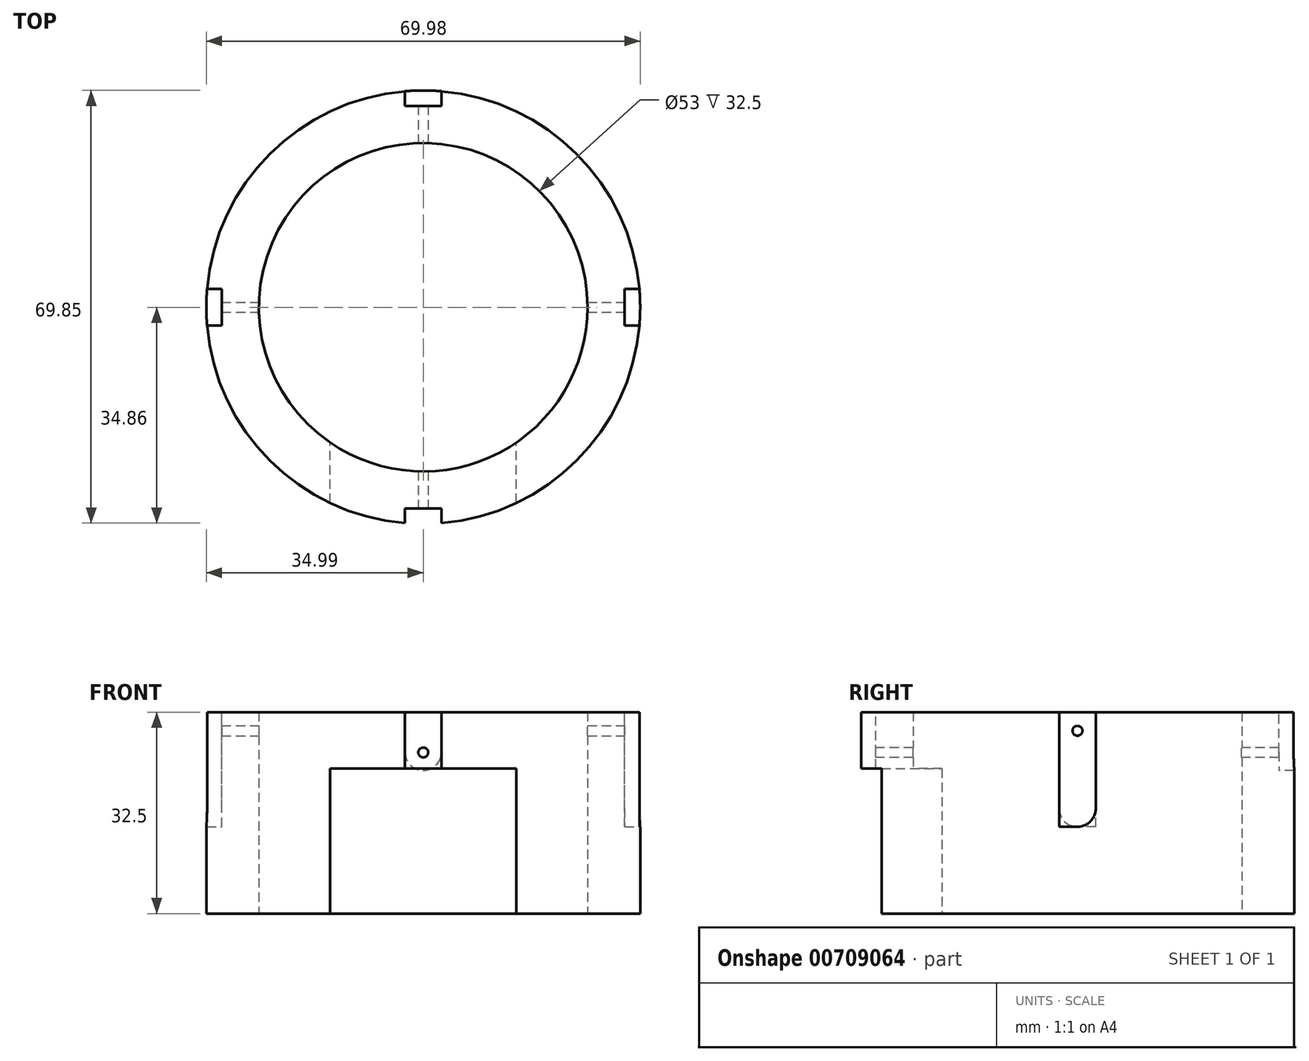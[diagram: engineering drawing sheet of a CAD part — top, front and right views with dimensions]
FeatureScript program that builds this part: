
annotation { "Feature Type Name" : "Feature", "Feature Type Description" : "" }
export const myFeature = defineFeature(function(context is Context, id is Id, definition is map)
    precondition{}
    {
        {
            var Q0;
            Q0=qCreatedBy(makeId("Top.planeOp"),FACE);
            var sketch = newSketch(context, id + "F0", { "sketchPlane" : qUnion([Q0])});
            skCircle(sketch, "E0", {"center": v(0, 0) * mm, "radius": 34.98 * mm});
            skCircle(sketch, "E1", {"center": v(0, 0) * mm, "radius": 26.5 * mm});
            skSolve(sketch);
        }
        {
            var Q0;
            Q0=makeQuery(id+"F0.imprint","IMPRINT",FACE,{"disambiguationData":[TD([[makeQuery(id+"F0.imprint","IMPRINT",EDGE,{"derivedFrom":sQuery(id+"F0.wireOp",EDGE,"E0")}),1.0]])]});
            extrude(context, id + "F1", {"entities" : qUnion([Q0]), "depth" : 32.5 * mm, "offsetDistance" : 25 * mm});
        }
        {
            var Q0;
            Q0=makeQuery(id+"F1.opExtrude","CAP_FACE",FACE,{"disambiguationData":[OSD([sQuery(id+"F0.wireOp",EDGE,"E0"),sQuery(id+"F0.wireOp",EDGE,"E1")])],"isStart":true});
            var sketch = newSketch(context, id + "F2", { "sketchPlane" : qUnion([Q0])});
            skLineSegment(sketch, "E2.bottom", {"start": v(-15.03, 49.64) * mm, "end": v(15.02, 49.64) * mm});
            skLineSegment(sketch, "E2.top", {"start": v(-15.03, 4.75) * mm, "end": v(15.03, 4.75) * mm});
            skLineSegment(sketch, "E2.left", {"start": v(-15.03, 49.64) * mm, "end": v(-15.03, 4.75) * mm});
            skLineSegment(sketch, "E2.right", {"start": v(15.02, 49.64) * mm, "end": v(15.03, 4.75) * mm});
            skSolve(sketch);
        }
        {
            var Q0;
            {var subQ0=sQuery(id+"F2.wireOp",EDGE,"E2.left");var subQ1=makeQuery(id+"F1.opExtrude","CAP_EDGE",EDGE,{"disambiguationData":[OSD([sQuery(id+"F0.wireOp",EDGE,"E0")])],"isStart":true});var subQ2=makeQuery(id+"F2.imprint","INTERSECT",VERTEX,{"derivedFrom":[subQ1,subQ0]});Q0=makeQuery(id+"F2.imprint","IMPRINT",FACE,{"disambiguationData":[TD([[makeQuery(id+"F2.imprint","IMPRINT",EDGE,{"disambiguationData":[TD([[subQ2,-1.0]])],"derivedFrom":subQ0}),1.0]])]});}
            extrude(context, id + "F3", {"entities" : qUnion([Q0]), "operationType" : NewBodyOperationType.REMOVE, "oppositeDirection" : true, "depth" : 23.4 * mm, "offsetDistance" : 25 * mm});
        }
        {
            var Q0;
            Q0=makeQuery(id+"F1.opExtrude","CAP_FACE",FACE,{"disambiguationData":[OSD([sQuery(id+"F0.wireOp",EDGE,"E0"),sQuery(id+"F0.wireOp",EDGE,"E1")])],"isStart":false});
            var sketch = newSketch(context, id + "F4", { "sketchPlane" : qUnion([Q0])});
            skLineSegment(sketch, "E3.bottom", {"start": v(-41.98, 2.95) * mm, "end": v(-32.5, 2.95) * mm});
            skLineSegment(sketch, "E3.top", {"start": v(-41.98, -2.95) * mm, "end": v(-32.5, -2.95) * mm});
            skLineSegment(sketch, "E3.left", {"start": v(-41.98, 2.95) * mm, "end": v(-41.98, -2.95) * mm});
            skLineSegment(sketch, "E3.right", {"start": v(-32.5, 2.95) * mm, "end": v(-32.5, -2.95) * mm});
            skLineSegment(sketch, "E4.bottom", {"start": v(32.5, 2.95) * mm, "end": v(40.96, 2.95) * mm});
            skLineSegment(sketch, "E4.top", {"start": v(32.5, -2.95) * mm, "end": v(40.96, -2.95) * mm});
            skLineSegment(sketch, "E4.left", {"start": v(32.5, 2.95) * mm, "end": v(32.5, -2.95) * mm});
            skLineSegment(sketch, "E4.right", {"start": v(40.96, 2.95) * mm, "end": v(40.96, -2.95) * mm});
            skSolve(sketch);
        }
        {
            var Q0;
            {var subQ0=sQuery(id+"F4.wireOp",EDGE,"E4.left");Q0=makeQuery(id+"F4.imprint","IMPRINT",FACE,{"disambiguationData":[TD([[makeQuery(id+"F4.imprint","IMPRINT",EDGE,{"derivedFrom":subQ0}),1.0]])]});}
            var Q1;
            {var subQ0=sQuery(id+"F4.wireOp",EDGE,"E3.right");Q1=makeQuery(id+"F4.imprint","IMPRINT",FACE,{"disambiguationData":[TD([[makeQuery(id+"F4.imprint","IMPRINT",EDGE,{"derivedFrom":subQ0}),-1.0]])]});}
            extrude(context, id + "F5", {"entities" : qUnion([Q0, Q1]), "operationType" : NewBodyOperationType.REMOVE, "oppositeDirection" : true, "depth" : 18.5 * mm, "offsetDistance" : 25 * mm});
        }
        {
            var Q0;
            Q0=makeQuery(id+"F5.boolean.opBoolean","COPY",EDGE,{"derivedFrom":makeQuery(id+"F5.opExtrude","CAP_EDGE",EDGE,{"disambiguationData":[OSD([sQuery(id+"F4.wireOp",EDGE,"E3.top")])],"isStart":false})});
            var Q1;
            Q1=makeQuery(id+"F5.boolean.opBoolean","COPY",EDGE,{"derivedFrom":makeQuery(id+"F5.opExtrude","CAP_EDGE",EDGE,{"disambiguationData":[OSD([sQuery(id+"F4.wireOp",EDGE,"E4.bottom")])],"isStart":false})});
            fillet(context, id + "F6", {"entities" : qUnion([Q0, Q1]), "radius" : 2.95 * mm, "tangentPropagation" : true, "allowEdgeOverflow" : false});
        }
        {
            var Q0;
            Q0=qCreatedBy(makeId("Right.planeOp"),FACE);
            var sketch = newSketch(context, id + "F7", { "sketchPlane" : qUnion([Q0])});
            skCircle(sketch, "E5", {"center": v(0, 29.5) * mm, "radius": 0.8 * mm});
            skSolve(sketch);
        }
        {
            var Q0;
            Q0 = qSketchRegion(id + "F7", true);
            extrude(context, id + "F8", {"entities" : qUnion([Q0]), "operationType" : NewBodyOperationType.REMOVE, "endBound" : BoundingType.THROUGH_ALL, "oppositeDirection" : true, "depth" : 25 * mm, "offsetDistance" : 25 * mm, "hasSecondDirection" : true, "secondDirectionBound" : SecondDirectionBoundingType.THROUGH_ALL, "secondDirectionOppositeDirection" : false, "secondDirectionDepth" : 25 * mm});
        }
        {
            var Q0;
            Q0=makeQuery(id+"F1.opExtrude","CAP_FACE",FACE,{"disambiguationData":[OSD([sQuery(id+"F0.wireOp",EDGE,"E0"),sQuery(id+"F0.wireOp",EDGE,"E1")])],"isStart":false});
            var sketch = newSketch(context, id + "F9", { "sketchPlane" : qUnion([Q0])});
            skLineSegment(sketch, "E6.bottom", {"start": v(-2.95, 38.61) * mm, "end": v(2.95, 38.61) * mm});
            skLineSegment(sketch, "E6.top", {"start": v(-2.95, 32.5) * mm, "end": v(2.95, 32.5) * mm});
            skLineSegment(sketch, "E6.left", {"start": v(-2.95, 38.61) * mm, "end": v(-2.95, 32.5) * mm});
            skLineSegment(sketch, "E6.right", {"start": v(2.95, 38.61) * mm, "end": v(2.95, 32.5) * mm});
            skLineSegment(sketch, "E7.bottom", {"start": v(-2.95, -39.44) * mm, "end": v(2.95, -39.44) * mm});
            skLineSegment(sketch, "E7.top", {"start": v(-2.95, -32.5) * mm, "end": v(2.95, -32.5) * mm});
            skLineSegment(sketch, "E7.left", {"start": v(-2.95, -39.44) * mm, "end": v(-2.95, -32.5) * mm});
            skLineSegment(sketch, "E7.right", {"start": v(2.95, -39.44) * mm, "end": v(2.95, -32.5) * mm});
            skSolve(sketch);
        }
        {
            var Q0;
            {var subQ0=sQuery(id+"F9.wireOp",EDGE,"E6.top");Q0=makeQuery(id+"F9.imprint","IMPRINT",FACE,{"disambiguationData":[TD([[makeQuery(id+"F9.imprint","IMPRINT",EDGE,{"derivedFrom":subQ0}),1.0]])]});}
            var Q1;
            {var subQ0=sQuery(id+"F9.wireOp",EDGE,"E7.top");Q1=makeQuery(id+"F9.imprint","IMPRINT",FACE,{"disambiguationData":[TD([[makeQuery(id+"F9.imprint","IMPRINT",EDGE,{"derivedFrom":subQ0}),-1.0]])]});}
            extrude(context, id + "F10", {"entities" : qUnion([Q0, Q1]), "operationType" : NewBodyOperationType.REMOVE, "oppositeDirection" : true, "depth" : 9.4 * mm, "offsetDistance" : 25 * mm});
        }
        {
            var Q0;
            Q0=makeQuery(id+"F10.boolean.opBoolean","COPY",EDGE,{"derivedFrom":makeQuery(id+"F10.opExtrude","CAP_EDGE",EDGE,{"disambiguationData":[OSD([sQuery(id+"F9.wireOp",EDGE,"E6.left")])],"isStart":false})});
            var Q1;
            Q1=makeQuery(id+"F10.boolean.opBoolean","COPY",EDGE,{"derivedFrom":makeQuery(id+"F10.opExtrude","CAP_EDGE",EDGE,{"disambiguationData":[OSD([sQuery(id+"F9.wireOp",EDGE,"E6.right")])],"isStart":false})});
            fillet(context, id + "F11", {"entities" : qUnion([Q0, Q1]), "radius" : 2.95 * mm, "tangentPropagation" : true, "allowEdgeOverflow" : false});
        }
        {
            var Q0;
            Q0=qCreatedBy(makeId("Front.planeOp"),FACE);
            var sketch = newSketch(context, id + "F12", { "sketchPlane" : qUnion([Q0])});
            skCircle(sketch, "E8", {"center": v(0, 26) * mm, "radius": 0.8 * mm});
            skSolve(sketch);
        }
        {
            var Q0;
            Q0=makeQuery(id+"F12.imprint","IMPRINT",FACE,{"disambiguationData":[TD([[makeQuery(id+"F12.imprint","IMPRINT",EDGE,{"derivedFrom":sQuery(id+"F12.wireOp",EDGE,"E8")}),1.0]])]});
            extrude(context, id + "F13", {"entities" : qUnion([Q0]), "operationType" : NewBodyOperationType.REMOVE, "endBound" : BoundingType.THROUGH_ALL, "oppositeDirection" : true, "depth" : 25 * mm, "offsetDistance" : 25 * mm, "hasSecondDirection" : true, "secondDirectionBound" : SecondDirectionBoundingType.THROUGH_ALL, "secondDirectionOppositeDirection" : false, "secondDirectionDepth" : 25 * mm});
        }
    });
